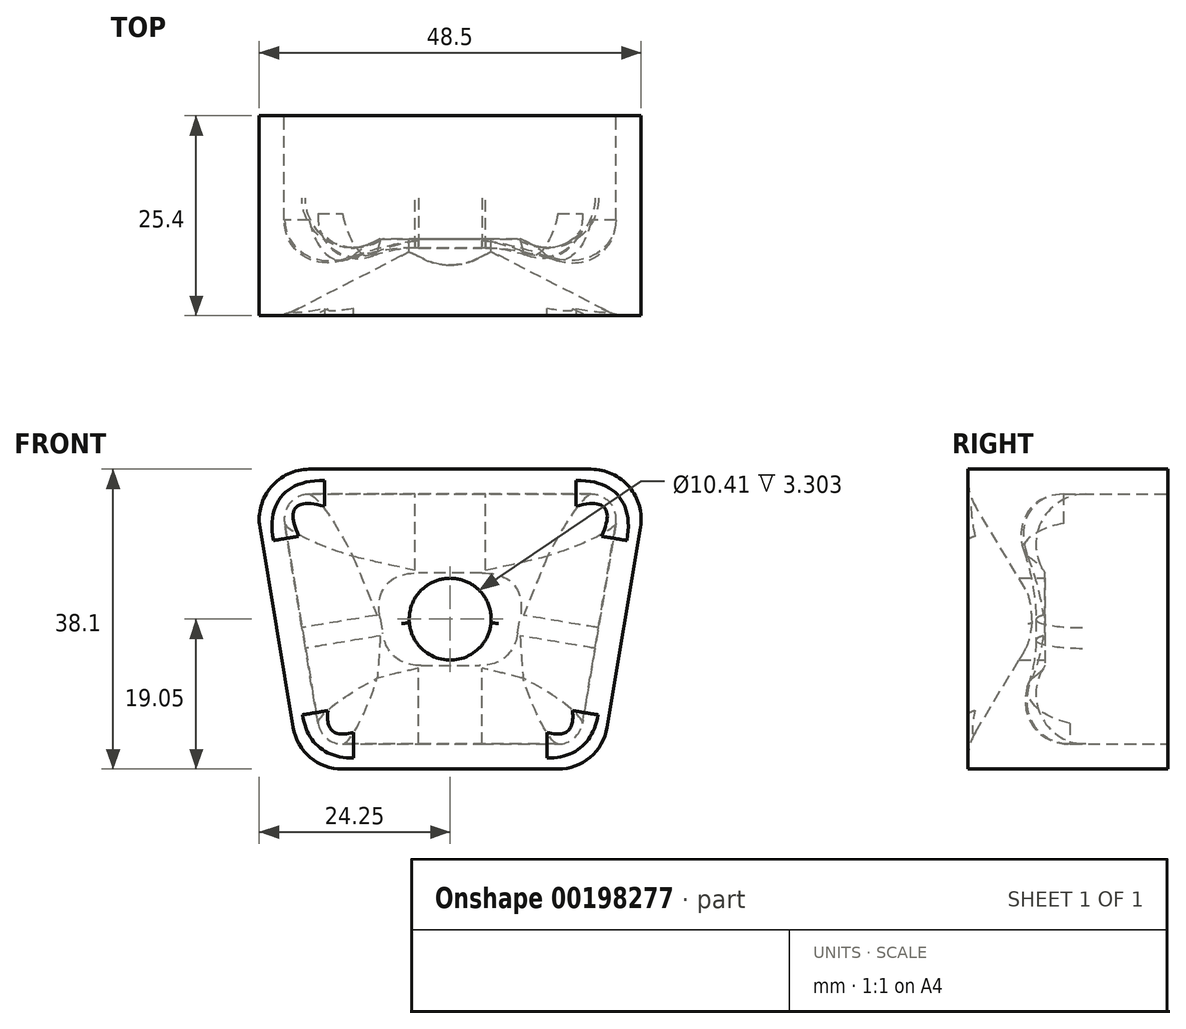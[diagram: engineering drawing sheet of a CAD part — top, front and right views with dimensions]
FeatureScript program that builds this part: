
annotation { "Feature Type Name" : "Feature", "Feature Type Description" : "" }
export const myFeature = defineFeature(function(context is Context, id is Id, definition is map)
    precondition{}
    {
        {
            var Q0;
            Q0=qCreatedBy(makeId("Front.planeOp"),FACE);
            var sketch = newSketch(context, id + "F0", { "sketchPlane" : qUnion([Q0])});
            skLineSegment(sketch, "E0.bottom", {"start": v(13.67, -19.05) * mm, "end": v(-13.67, -19.05) * mm});
            skPoint(sketch, "E0.middle", {"position": v(0, 0) * mm});
            skLineSegment(sketch, "E1", {"start": v(-17.9, 19.05) * mm, "end": v(17.9, 19.05) * mm});
            skLineSegment(sketch, "E2", {"start": v(24.17, 11.66) * mm, "end": v(19.93, -13.74) * mm});
            skLineSegment(sketch, "E3", {"start": v(-24.17, 11.66) * mm, "end": v(-19.93, -13.74) * mm});
            skPoint(sketch, "E4.visualSharp", {"position": v(-25.4, 19.05) * mm});
            skArc(sketch, "E4.filletArc", {"start": v(-17.9, 19.05) * mm, "mid": v(-22.75, 16.8) * mm, "end": v(-24.17, 11.66) * mm});
            skPoint(sketch, "E5.visualSharp", {"position": v(25.4, 19.05) * mm});
            skArc(sketch, "E5.filletArc", {"start": v(24.17, 11.66) * mm, "mid": v(22.75, 16.8) * mm, "end": v(17.9, 19.05) * mm});
            skPoint(sketch, "E6.visualSharp", {"position": v(19.05, -19.05) * mm});
            skArc(sketch, "E6.filletArc", {"start": v(13.67, -19.05) * mm, "mid": v(17.78, -17.55) * mm, "end": v(19.93, -13.74) * mm});
            skPoint(sketch, "E7.visualSharp", {"position": v(-19.05, -19.05) * mm});
            skArc(sketch, "E7.filletArc", {"start": v(-19.93, -13.74) * mm, "mid": v(-17.78, -17.55) * mm, "end": v(-13.67, -19.05) * mm});
            skSolve(sketch);
        }
        {
            var Q0;
            Q0 = qSketchRegion(id + "F0", true);
            extrude(context, id + "F1", {"entities" : qUnion([Q0]), "depth" : 25.4 * mm});
        }
        {
            var Q0;
            Q0=makeQuery(id+"F1.opExtrude","CAP_FACE",FACE,{"disambiguationData":[OSD([sQuery(id+"F0.wireOp",EDGE,"E0.bottom"),sQuery(id+"F0.wireOp",EDGE,"E1"),sQuery(id+"F0.wireOp",EDGE,"E2"),sQuery(id+"F0.wireOp",EDGE,"E3"),sQuery(id+"F0.wireOp",EDGE,"E4.filletArc"),sQuery(id+"F0.wireOp",EDGE,"E5.filletArc"),sQuery(id+"F0.wireOp",EDGE,"E6.filletArc"),sQuery(id+"F0.wireOp",EDGE,"E7.filletArc")])],"isStart":false});
            var sketch = newSketch(context, id + "F2", { "sketchPlane" : qUnion([Q0])});
            skLineSegment(sketch, "E8.0.0", {"start": v(-13.67, -19.05) * mm, "end": v(13.67, -19.05) * mm});
            skArc(sketch, "E8.0.1", {"start": v(13.67, -19.05) * mm, "mid": v(17.78, -17.55) * mm, "end": v(19.93, -13.74) * mm});
            skLineSegment(sketch, "E8.0.2", {"start": v(19.93, -13.74) * mm, "end": v(24.17, 11.66) * mm});
            skArc(sketch, "E8.0.3", {"start": v(24.17, 11.66) * mm, "mid": v(22.75, 16.8) * mm, "end": v(17.9, 19.05) * mm});
            skLineSegment(sketch, "E8.0.4", {"start": v(17.9, 19.05) * mm, "end": v(-17.9, 19.05) * mm});
            skArc(sketch, "E8.0.5", {"start": v(-17.9, 19.05) * mm, "mid": v(-22.75, 16.8) * mm, "end": v(-24.17, 11.66) * mm});
            skLineSegment(sketch, "E8.0.6", {"start": v(-24.17, 11.66) * mm, "end": v(-19.93, -13.74) * mm});
            skArc(sketch, "E8.0.7", {"start": v(-19.93, -13.74) * mm, "mid": v(-17.78, -17.55) * mm, "end": v(-13.67, -19.05) * mm});
            skLineSegment(sketch, "E9.0", {"start": v(21.65, 15.88) * mm, "end": v(-21.65, 15.87) * mm});
            skLineSegment(sketch, "E9.1", {"start": v(16.36, -15.88) * mm, "end": v(21.65, 15.88) * mm});
            skLineSegment(sketch, "E9.2", {"start": v(-16.36, -15.88) * mm, "end": v(16.36, -15.88) * mm});
            skLineSegment(sketch, "E9.3", {"start": v(-21.65, 15.88) * mm, "end": v(-16.36, -15.88) * mm});
            skSolve(sketch);
        }
        {
            var Q0;
            Q0=makeQuery(id+"F2.imprint","IMPRINT",FACE,{"disambiguationData":[TD([[makeQuery(id+"F2.imprint","IMPRINT",EDGE,{"derivedFrom":sQuery(id+"F2.wireOp",EDGE,"E9.0")}),1.0]])]});
            extrude(context, id + "F3", {"entities" : qUnion([Q0]), "operationType" : NewBodyOperationType.REMOVE, "oppositeDirection" : true, "depth" : 9.52 * mm});
        }
        {
            var Q0;
            Q0=makeQuery(id+"F3.boolean.opBoolean","COPY",EDGE,{"derivedFrom":makeQuery(id+"F3.opExtrude","CAP_EDGE",EDGE,{"disambiguationData":[OSD([sQuery(id+"F2.wireOp",EDGE,"E9.3")])],"isStart":false})});
            var Q1;
            Q1=makeQuery(id+"F3.boolean.opBoolean","COPY",EDGE,{"derivedFrom":makeQuery(id+"F3.opExtrude","CAP_EDGE",EDGE,{"disambiguationData":[OSD([sQuery(id+"F2.wireOp",EDGE,"E9.0")])],"isStart":false})});
            var Q2;
            Q2=makeQuery(id+"F3.boolean.opBoolean","COPY",EDGE,{"derivedFrom":makeQuery(id+"F3.opExtrude","CAP_EDGE",EDGE,{"disambiguationData":[OSD([sQuery(id+"F2.wireOp",EDGE,"E9.1")])],"isStart":false})});
            var Q3;
            Q3=makeQuery(id+"F3.boolean.opBoolean","COPY",EDGE,{"derivedFrom":makeQuery(id+"F3.opExtrude","CAP_EDGE",EDGE,{"disambiguationData":[OSD([sQuery(id+"F2.wireOp",EDGE,"E9.2")])],"isStart":false})});
            chamfer(context, id + "F4", {"entities" : qUnion([Q0, Q1, Q2, Q3]), "chamferType" : ChamferType.TWO_OFFSETS, "width1" : 15.75 * mm, "oppositeDirection" : false, "width2" : 9.52 * mm, "tangentPropagation" : true});
        }
        {
            var Q0;
            Q0=makeQuery(id+"F4.opChamfer","BLEND_EDGE",EDGE,{"blendedFrom":[makeQuery(id+"F3.boolean.opBoolean","COPY",EDGE,{"derivedFrom":makeQuery(id+"F3.opExtrude","CAP_EDGE",EDGE,{"disambiguationData":[OSD([sQuery(id+"F2.wireOp",EDGE,"E9.0")])],"isStart":false})}),makeQuery(id+"F3.boolean.opBoolean","COPY",EDGE,{"derivedFrom":makeQuery(id+"F3.opExtrude","CAP_EDGE",EDGE,{"disambiguationData":[OSD([sQuery(id+"F2.wireOp",EDGE,"E9.3")])],"isStart":false})})],"blendedInto":[]});
            var Q1;
            Q1=makeQuery(id+"F4.opChamfer","BLEND_EDGE",EDGE,{"blendedFrom":[makeQuery(id+"F3.boolean.opBoolean","COPY",EDGE,{"derivedFrom":makeQuery(id+"F3.opExtrude","CAP_EDGE",EDGE,{"disambiguationData":[OSD([sQuery(id+"F2.wireOp",EDGE,"E9.0")])],"isStart":false})}),makeQuery(id+"F3.boolean.opBoolean","COPY",EDGE,{"derivedFrom":makeQuery(id+"F3.opExtrude","CAP_EDGE",EDGE,{"disambiguationData":[OSD([sQuery(id+"F2.wireOp",EDGE,"E9.1")])],"isStart":false})})],"blendedInto":[]});
            var Q2;
            Q2=makeQuery(id+"F4.opChamfer","BLEND_EDGE",EDGE,{"blendedFrom":[makeQuery(id+"F3.boolean.opBoolean","COPY",EDGE,{"derivedFrom":makeQuery(id+"F3.opExtrude","CAP_EDGE",EDGE,{"disambiguationData":[OSD([sQuery(id+"F2.wireOp",EDGE,"E9.2")])],"isStart":false})}),makeQuery(id+"F3.boolean.opBoolean","COPY",EDGE,{"derivedFrom":makeQuery(id+"F3.opExtrude","CAP_EDGE",EDGE,{"disambiguationData":[OSD([sQuery(id+"F2.wireOp",EDGE,"E9.3")])],"isStart":false})})],"blendedInto":[]});
            var Q3;
            Q3=makeQuery(id+"F4.opChamfer","BLEND_EDGE",EDGE,{"blendedFrom":[makeQuery(id+"F3.boolean.opBoolean","COPY",EDGE,{"derivedFrom":makeQuery(id+"F3.opExtrude","CAP_EDGE",EDGE,{"disambiguationData":[OSD([sQuery(id+"F2.wireOp",EDGE,"E9.1")])],"isStart":false})}),makeQuery(id+"F3.boolean.opBoolean","COPY",EDGE,{"derivedFrom":makeQuery(id+"F3.opExtrude","CAP_EDGE",EDGE,{"disambiguationData":[OSD([sQuery(id+"F2.wireOp",EDGE,"E9.2")])],"isStart":false})})],"blendedInto":[]});
            fillet(context, id + "F5", {"entities" : qUnion([Q0, Q1, Q2, Q3]), "radius" : 6.35 * mm, "tangentPropagation" : true, "allowEdgeOverflow" : false});
        }
        {
            var Q0;
            Q0=makeQuery(id+"F4.opChamfer","BLEND_EDGE",EDGE,{"blendedFrom":[makeQuery(id+"F3.boolean.opBoolean","COPY",EDGE,{"derivedFrom":makeQuery(id+"F3.opExtrude","CAP_EDGE",EDGE,{"disambiguationData":[OSD([sQuery(id+"F2.wireOp",EDGE,"E9.3")])],"isStart":false})}),makeQuery(id+"F1.opExtrude","CAP_FACE",FACE,{"disambiguationData":[OSD([sQuery(id+"F0.wireOp",EDGE,"E0.bottom"),sQuery(id+"F0.wireOp",EDGE,"E1"),sQuery(id+"F0.wireOp",EDGE,"E2"),sQuery(id+"F0.wireOp",EDGE,"E3"),sQuery(id+"F0.wireOp",EDGE,"E4.filletArc"),sQuery(id+"F0.wireOp",EDGE,"E5.filletArc"),sQuery(id+"F0.wireOp",EDGE,"E6.filletArc"),sQuery(id+"F0.wireOp",EDGE,"E7.filletArc")])],"isStart":false})],"blendedInto":[makeQuery(id+"F1.opExtrude","CAP_FACE",FACE,{"disambiguationData":[OSD([sQuery(id+"F0.wireOp",EDGE,"E0.bottom"),sQuery(id+"F0.wireOp",EDGE,"E1"),sQuery(id+"F0.wireOp",EDGE,"E2"),sQuery(id+"F0.wireOp",EDGE,"E3"),sQuery(id+"F0.wireOp",EDGE,"E4.filletArc"),sQuery(id+"F0.wireOp",EDGE,"E5.filletArc"),sQuery(id+"F0.wireOp",EDGE,"E6.filletArc"),sQuery(id+"F0.wireOp",EDGE,"E7.filletArc")])],"isStart":false})]});
            fillet(context, id + "F6", {"entities" : qUnion([Q0]), "radius" : 6.35 * mm, "tangentPropagation" : true, "allowEdgeOverflow" : false});
        }
        {
            var Q0;
            Q0=makeQuery(id+"F1.opExtrude","CAP_FACE",FACE,{"disambiguationData":[OSD([sQuery(id+"F0.wireOp",EDGE,"E0.bottom"),sQuery(id+"F0.wireOp",EDGE,"E1"),sQuery(id+"F0.wireOp",EDGE,"E2"),sQuery(id+"F0.wireOp",EDGE,"E3"),sQuery(id+"F0.wireOp",EDGE,"E4.filletArc"),sQuery(id+"F0.wireOp",EDGE,"E5.filletArc"),sQuery(id+"F0.wireOp",EDGE,"E6.filletArc"),sQuery(id+"F0.wireOp",EDGE,"E7.filletArc")])],"isStart":true});
            shell(context, id + "F7", {"entities" : qUnion([Q0]), "thickness" : 3.17 * mm});
        }
        {
            var Q0;
            Q0=makeQuery(id+"F7.opShell","TWEAK_EDGE",EDGE,{"derivedFrom":[makeQuery(id+"F1.opExtrude","SWEPT_FACE",FACE,{"disambiguationData":[OSD([sQuery(id+"F0.wireOp",EDGE,"E1")])]}),makeQuery(id+"F4.opChamfer","BLEND_FACE",FACE,{"disambiguationData":[OSD([sQuery(id+"F2.wireOp",EDGE,"E9.0")])]})]});
            fillet(context, id + "F8", {"entities" : qUnion([Q0]), "radius" : 6.35 * mm, "tangentPropagation" : true, "allowEdgeOverflow" : false});
        }
        {
            var Q0;
            Q0=makeQuery(id+"F7.opShell","OFFSET_FACE",FACE,{"disambiguationData":[OSD([sQuery(id+"F2.wireOp",EDGE,"E9.0"),sQuery(id+"F2.wireOp",EDGE,"E9.1"),sQuery(id+"F2.wireOp",EDGE,"E9.2"),sQuery(id+"F2.wireOp",EDGE,"E9.3")])]});
            var sketch = newSketch(context, id + "F9", { "sketchPlane" : qUnion([Q0])});
            skCircle(sketch, "E10", {"center": v(0, 0) * mm, "radius": 5.2 * mm});
            skCircle(sketch, "E11", {"center": v(0, 0) * mm, "radius": 12.7 * mm});
            skSolve(sketch);
        }
        {
            var Q0;
            Q0=makeQuery(id+"F9.imprint","IMPRINT",FACE,{"disambiguationData":[TD([[makeQuery(id+"F9.imprint","IMPRINT",EDGE,{"derivedFrom":sQuery(id+"F9.wireOp",EDGE,"E10")}),1.0]])]});
            var Q1;
            {var subQ0=sQuery(id+"F2.wireOp",EDGE,"E9.3");var subQ1=sQuery(id+"F2.wireOp",EDGE,"E9.2");var subQ2=sQuery(id+"F2.wireOp",EDGE,"E9.1");var subQ3=sQuery(id+"F2.wireOp",EDGE,"E9.0");var subQ4=makeQuery(id+"F3.boolean.opBoolean","COPY",FACE,{"derivedFrom":makeQuery(id+"F3.opExtrude","CAP_FACE",FACE,{"disambiguationData":[OSD([subQ3,subQ2,subQ1,subQ0])],"isStart":false})});var subQ5=makeQuery(id+"F3.boolean.opBoolean","COPY",EDGE,{"derivedFrom":makeQuery(id+"F3.opExtrude","CAP_EDGE",EDGE,{"disambiguationData":[OSD([subQ2])],"isStart":false})});var subQ6=makeQuery(id+"F3.boolean.opBoolean","COPY",EDGE,{"derivedFrom":makeQuery(id+"F3.opExtrude","CAP_EDGE",EDGE,{"disambiguationData":[OSD([subQ3])],"isStart":false})});Q1=makeQuery(id+"F9.imprint","IMPRINT",FACE,{"disambiguationData":[TD([[makeQuery(id+"F9.imprint","IMPRINT",EDGE,{"derivedFrom":makeQuery(id+"F7.opShell","OFFSET_EDGE",EDGE,{"disambiguationData":[OSD([subQ3,subQ2,subQ1,subQ0]),TDD([makeQuery(id+"F5.opFillet","BLEND_EDGE",EDGE,{"blendedFrom":[makeQuery(id+"F4.opChamfer","BLEND_EDGE",EDGE,{"blendedFrom":[subQ6,subQ5],"blendedInto":[]}),subQ4],"blendedInto":[subQ4]})])]})}),-1.0]])]});}
            extrude(context, id + "F10", {"entities" : qUnion([Q0, Q1]), "operationType" : NewBodyOperationType.REMOVE, "endBound" : BoundingType.THROUGH_ALL, "oppositeDirection" : true, "depth" : 25.4 * mm});
        }
        {
            var Q0;
            Q0=makeQuery(id+"F9.imprint","IMPRINT",FACE,{"disambiguationData":[TD([[makeQuery(id+"F9.imprint","IMPRINT",EDGE,{"derivedFrom":sQuery(id+"F9.wireOp",EDGE,"E11")}),1.0]])]});
            var Q1;
            {var subQ0=sQuery(id+"F9.wireOp",EDGE,"E10");var subQ1=sQuery(id+"F2.wireOp",EDGE,"E9.3");var subQ2=sQuery(id+"F2.wireOp",EDGE,"E9.2");var subQ3=sQuery(id+"F2.wireOp",EDGE,"E9.1");var subQ4=sQuery(id+"F2.wireOp",EDGE,"E9.0");var subQ5=makeQuery(id+"F3.boolean.opBoolean","COPY",FACE,{"derivedFrom":makeQuery(id+"F3.opExtrude","CAP_FACE",FACE,{"disambiguationData":[OSD([subQ4,subQ3,subQ2,subQ1])],"isStart":false})});var subQ6=makeQuery(id+"F3.boolean.opBoolean","COPY",EDGE,{"derivedFrom":makeQuery(id+"F3.opExtrude","CAP_EDGE",EDGE,{"disambiguationData":[OSD([subQ4])],"isStart":false})});var subQ7=makeQuery(id+"F7.opShell","OFFSET_EDGE",EDGE,{"disambiguationData":[OSD([subQ4,subQ3,subQ2,subQ1]),TDD([makeQuery(id+"F5.opFillet","BLEND_EDGE",EDGE,{"blendedFrom":[makeQuery(id+"F4.opChamfer","BLEND_EDGE",EDGE,{"blendedFrom":[subQ6,makeQuery(id+"F3.boolean.opBoolean","COPY",EDGE,{"derivedFrom":makeQuery(id+"F3.opExtrude","CAP_EDGE",EDGE,{"disambiguationData":[OSD([subQ3])],"isStart":false})})],"blendedInto":[]}),subQ5],"blendedInto":[subQ5]})])]});var subQ8=makeQuery(id+"F9.imprint","INTERSECT",VERTEX,{"derivedFrom":[subQ7,subQ0]});Q1=makeQuery(id+"F9.imprint","IMPRINT",FACE,{"disambiguationData":[TD([[makeQuery(id+"F9.imprint","IMPRINT",EDGE,{"disambiguationData":[TD([[subQ8,1.0]])],"derivedFrom":subQ0}),-1.0]])]});}
            var Q2;
            {var subQ0=sQuery(id+"F9.wireOp",EDGE,"E10");var subQ1=sQuery(id+"F2.wireOp",EDGE,"E9.3");var subQ2=sQuery(id+"F2.wireOp",EDGE,"E9.2");var subQ3=sQuery(id+"F2.wireOp",EDGE,"E9.1");var subQ4=sQuery(id+"F2.wireOp",EDGE,"E9.0");var subQ5=makeQuery(id+"F3.boolean.opBoolean","COPY",FACE,{"derivedFrom":makeQuery(id+"F3.opExtrude","CAP_FACE",FACE,{"disambiguationData":[OSD([subQ4,subQ3,subQ2,subQ1])],"isStart":false})});var subQ6=makeQuery(id+"F3.boolean.opBoolean","COPY",EDGE,{"derivedFrom":makeQuery(id+"F3.opExtrude","CAP_EDGE",EDGE,{"disambiguationData":[OSD([subQ2])],"isStart":false})});var subQ7=makeQuery(id+"F7.opShell","OFFSET_EDGE",EDGE,{"disambiguationData":[OSD([subQ4,subQ3,subQ2,subQ1]),TDD([makeQuery(id+"F5.opFillet","BLEND_EDGE",EDGE,{"blendedFrom":[makeQuery(id+"F4.opChamfer","BLEND_EDGE",EDGE,{"blendedFrom":[makeQuery(id+"F3.boolean.opBoolean","COPY",EDGE,{"derivedFrom":makeQuery(id+"F3.opExtrude","CAP_EDGE",EDGE,{"disambiguationData":[OSD([subQ3])],"isStart":false})}),subQ6],"blendedInto":[]}),subQ5],"blendedInto":[subQ5]})])]});var subQ8=makeQuery(id+"F9.imprint","INTERSECT",VERTEX,{"derivedFrom":[subQ7,subQ0]});Q2=makeQuery(id+"F9.imprint","IMPRINT",FACE,{"disambiguationData":[TD([[makeQuery(id+"F9.imprint","IMPRINT",EDGE,{"disambiguationData":[TD([[subQ8,-1.0]])],"derivedFrom":subQ0}),-1.0]])]});}
            extrude(context, id + "F11", {"entities" : qUnion([Q0, Q1, Q2]), "operationType" : NewBodyOperationType.REMOVE, "oppositeDirection" : true, "depth" : 2.95 * mm});
        }
    });
